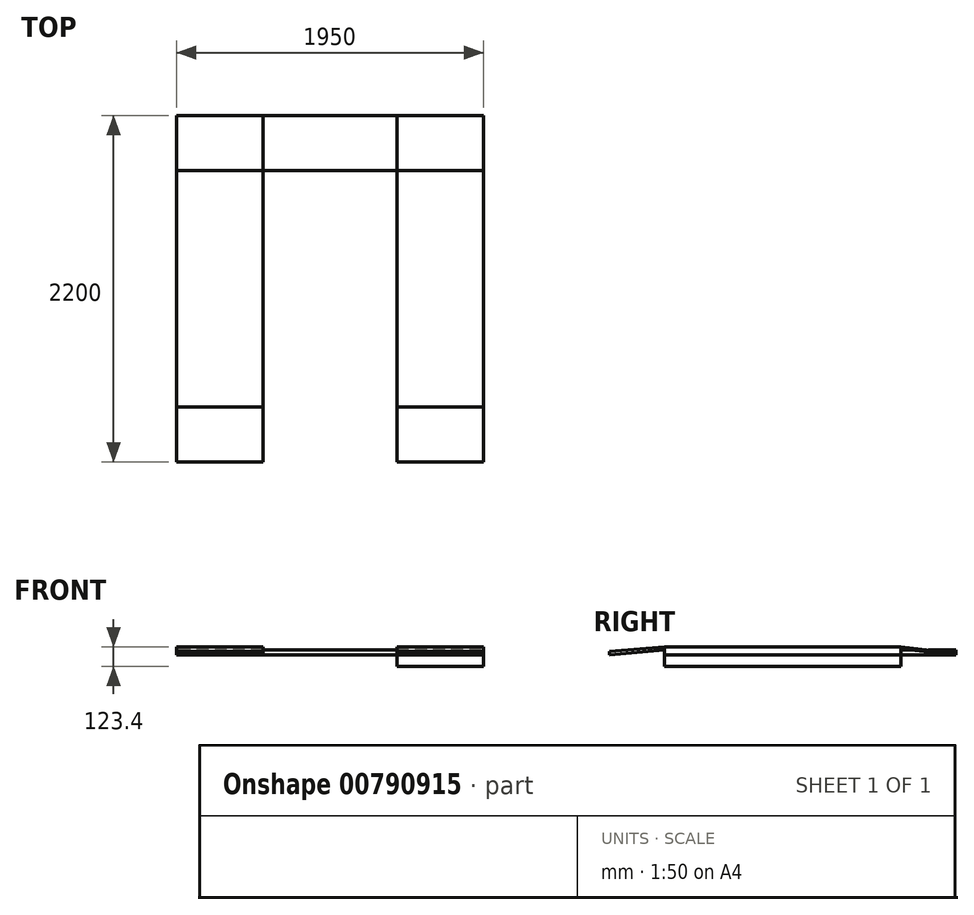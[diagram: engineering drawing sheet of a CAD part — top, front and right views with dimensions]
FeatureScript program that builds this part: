
annotation { "Feature Type Name" : "Feature", "Feature Type Description" : "" }
export const myFeature = defineFeature(function(context is Context, id is Id, definition is map)
    precondition{}
    {
        {
            var Q0;
            Q0=qCreatedBy(makeId("Top.planeOp"),FACE);
            var sketch = newSketch(context, id + "F0", { "sketchPlane" : qUnion([Q0])});
            skLineSegment(sketch, "E0.bottom", {"start": v(0, 0) * mm, "end": v(-550, 0) * mm});
            skLineSegment(sketch, "E0.top", {"start": v(0, 1500) * mm, "end": v(-550, 1500) * mm});
            skLineSegment(sketch, "E0.left", {"start": v(0, 0) * mm, "end": v(0, 1500) * mm});
            skLineSegment(sketch, "E0.right", {"start": v(-550, 0) * mm, "end": v(-550, 1500) * mm});
            skLineSegment(sketch, "E1.bottom", {"start": v(-550, 1500) * mm, "end": v(0, 1500) * mm});
            skLineSegment(sketch, "E1.top", {"start": v(-550, 1850) * mm, "end": v(0, 1850) * mm});
            skLineSegment(sketch, "E1.left", {"start": v(-550, 1500) * mm, "end": v(-550, 1850) * mm});
            skLineSegment(sketch, "E1.right", {"start": v(0, 1500) * mm, "end": v(0, 1850) * mm});
            skLineSegment(sketch, "E2.bottom", {"start": v(-550, 0) * mm, "end": v(0, 0) * mm});
            skLineSegment(sketch, "E2.top", {"start": v(-550, -350) * mm, "end": v(0, -350) * mm});
            skLineSegment(sketch, "E2.left", {"start": v(-550, 0) * mm, "end": v(-550, -350) * mm});
            skLineSegment(sketch, "E2.right", {"start": v(0, 0) * mm, "end": v(0, -350) * mm});
            skLineSegment(sketch, "E3.bottom", {"start": v(-1400, 0) * mm, "end": v(-1950, 0) * mm});
            skLineSegment(sketch, "E3.top", {"start": v(-1400, 1500) * mm, "end": v(-1950, 1500) * mm});
            skLineSegment(sketch, "E3.left", {"start": v(-1950, 0) * mm, "end": v(-1950, 1500) * mm});
            skLineSegment(sketch, "E3.right", {"start": v(-1400, 0) * mm, "end": v(-1400, 1500) * mm});
            skLineSegment(sketch, "E4.bottom", {"start": v(-1950, 1500) * mm, "end": v(-1400, 1500) * mm});
            skLineSegment(sketch, "E4.top", {"start": v(-1950, 1850) * mm, "end": v(-1400, 1850) * mm});
            skLineSegment(sketch, "E4.left", {"start": v(-1950, 1500) * mm, "end": v(-1950, 1850) * mm});
            skLineSegment(sketch, "E4.right", {"start": v(-1400, 1500) * mm, "end": v(-1400, 1850) * mm});
            skLineSegment(sketch, "E5.bottom", {"start": v(-1950, 0) * mm, "end": v(-1400, 0) * mm});
            skLineSegment(sketch, "E5.top", {"start": v(-1950, -350) * mm, "end": v(-1400, -350) * mm});
            skLineSegment(sketch, "E5.left", {"start": v(-1950, 0) * mm, "end": v(-1950, -350) * mm});
            skLineSegment(sketch, "E5.right", {"start": v(-1400, 0) * mm, "end": v(-1400, -350) * mm});
            skLineSegment(sketch, "E6.bottom", {"start": v(-1400, 1850) * mm, "end": v(-550, 1850) * mm});
            skLineSegment(sketch, "E6.top", {"start": v(-1400, 1500) * mm, "end": v(-550, 1500) * mm});
            skLineSegment(sketch, "E6.left", {"start": v(-1400, 1850) * mm, "end": v(-1400, 1500) * mm});
            skLineSegment(sketch, "E6.right", {"start": v(-550, 1850) * mm, "end": v(-550, 1500) * mm});
            skSolve(sketch);
        }
        {
            var Q0;
            Q0=makeQuery(id+"F0.imprint","IMPRINT",FACE,{"disambiguationData":[TD([[makeQuery(id+"F0.imprint","IMPRINT",EDGE,{"derivedFrom":sQuery(id+"F0.wireOp",EDGE,"E3.left")}),-1.0]])]});
            var Q1;
            Q1=makeQuery(id+"F0.imprint","IMPRINT",FACE,{"disambiguationData":[TD([[makeQuery(id+"F0.imprint","IMPRINT",EDGE,{"derivedFrom":sQuery(id+"F0.wireOp",EDGE,"E0.left")}),1.0]])]});
            extrude(context, id + "F1", {"entities" : qUnion([Q0, Q1]), "depth" : 50 * mm, "offsetDistance" : 25 * mm});
        }
        {
            var Q0;
            Q0=makeQuery(id+"F0.imprint","IMPRINT",FACE,{"disambiguationData":[TD([[makeQuery(id+"F0.imprint","IMPRINT",EDGE,{"derivedFrom":sQuery(id+"F0.wireOp",EDGE,"E6.bottom")}),-1.0]])]});
            extrude(context, id + "F2", {"entities" : qUnion([Q0]), "depth" : 30 * mm, "offsetDistance" : 25 * mm});
        }
        {
            var Q0;
            Q0=makeQuery(id+"F1.opExtrude","SWEPT_FACE",FACE,{"disambiguationData":[OSD([sQuery(id+"F0.wireOp",EDGE,"E0.left")])]});
            var sketch = newSketch(context, id + "F3", { "sketchPlane" : qUnion([Q0])});
            skLineSegment(sketch, "E7.0", {"start": v(0, 0) * mm, "end": v(-350, 0) * mm});
            skLineSegment(sketch, "E8.0", {"start": v(0, 50) * mm, "end": v(1500, 50) * mm});
            skLineSegment(sketch, "E9", {"start": v(-350, 0) * mm, "end": v(-350, 20) * mm});
            skLineSegment(sketch, "E10", {"start": v(-350, 20) * mm, "end": v(0, 50) * mm});
            skLineSegment(sketch, "E11", {"start": v(0, 50) * mm, "end": v(0, 30) * mm});
            skLineSegment(sketch, "E12", {"start": v(0, 30) * mm, "end": v(-350, 0) * mm});
            skLineSegment(sketch, "E13.bottom", {"start": v(0, 0) * mm, "end": v(1500, 0) * mm});
            skLineSegment(sketch, "E13.top", {"start": v(0, -73.4) * mm, "end": v(1500, -73.4) * mm});
            skLineSegment(sketch, "E13.left", {"start": v(0, 0) * mm, "end": v(0, -73.4) * mm});
            skLineSegment(sketch, "E13.right", {"start": v(1500, 0) * mm, "end": v(1500, -73.4) * mm});
            skLineSegment(sketch, "E14", {"start": v(1850, 0) * mm, "end": v(1850, 10) * mm});
            skLineSegment(sketch, "E15", {"start": v(1850, 10) * mm, "end": v(1500, 50) * mm});
            skLineSegment(sketch, "E16", {"start": v(1500, 35.74) * mm, "end": v(1850, 0) * mm});
            skPoint(sketch, "E17.0.start.orphan", {"position": v(1500, 0) * mm});
            skSolve(sketch);
        }
        {
            var Q0;
            Q0=makeQuery(id+"F3.imprint","IMPRINT",FACE,{"disambiguationData":[TD([[makeQuery(id+"F3.imprint","IMPRINT",EDGE,{"derivedFrom":sQuery(id+"F3.wireOp",EDGE,"E9")}),-1.0]])]});
            extrude(context, id + "F4", {"entities" : qUnion([Q0]), "operationType" : NewBodyOperationType.ADD, "oppositeDirection" : true, "depth" : 550 * mm, "offsetDistance" : 25 * mm});
        }
        {
            var Q0;
            Q0 = qSketchRegion(id + "F3", true);
            extrude(context, id + "F5", {"entities" : qUnion([Q0]), "oppositeDirection" : true, "depth" : 550 * mm, "offsetDistance" : 25 * mm});
        }
        {
            var Q0;
            Q0=makeQuery(id+"F3.imprint","IMPRINT",FACE,{"disambiguationData":[TD([[makeQuery(id+"F3.imprint","IMPRINT",EDGE,{"derivedFrom":sQuery(id+"F3.wireOp",EDGE,"E14")}),1.0]])]});
            extrude(context, id + "F6", {"entities" : qUnion([Q0]), "oppositeDirection" : true, "depth" : 550 * mm, "offsetDistance" : 25 * mm});
        }
        {
            var Q0;
            Q0=makeQuery(id+"F1.opExtrude","SWEPT_FACE",FACE,{"disambiguationData":[OSD([sQuery(id+"F0.wireOp",EDGE,"E3.left")])]});
            var sketch = newSketch(context, id + "F7", { "sketchPlane" : qUnion([Q0])});
            skLineSegment(sketch, "E18.0", {"start": v(0, 30) * mm, "end": v(350, 0) * mm});
            skLineSegment(sketch, "E19.0", {"start": v(350, 20) * mm, "end": v(0, 50) * mm});
            skPoint(sketch, "E20.0", {"position": v(350, 10) * mm});
            skLineSegment(sketch, "E21.0.0", {"start": v(-1500, 35.74) * mm, "end": v(-1500, 50) * mm});
            skLineSegment(sketch, "E21.0.1", {"start": v(-1500, 50) * mm, "end": v(-1850, 10) * mm});
            skLineSegment(sketch, "E21.0.2", {"start": v(-1850, 10) * mm, "end": v(-1850, 0) * mm});
            skLineSegment(sketch, "E21.0.3", {"start": v(-1850, 0) * mm, "end": v(-1500, 35.74) * mm});
            skLineSegment(sketch, "E22", {"start": v(350, 20) * mm, "end": v(350, 0) * mm});
            skLineSegment(sketch, "E23", {"start": v(0, 30) * mm, "end": v(0, 50) * mm});
            skSolve(sketch);
        }
        {
            var Q0;
            Q0 = qSketchRegion(id + "F7", true);
            extrude(context, id + "F8", {"entities" : qUnion([Q0]), "operationType" : NewBodyOperationType.ADD, "oppositeDirection" : true, "depth" : 549 * mm, "offsetDistance" : 25 * mm});
        }
    });
